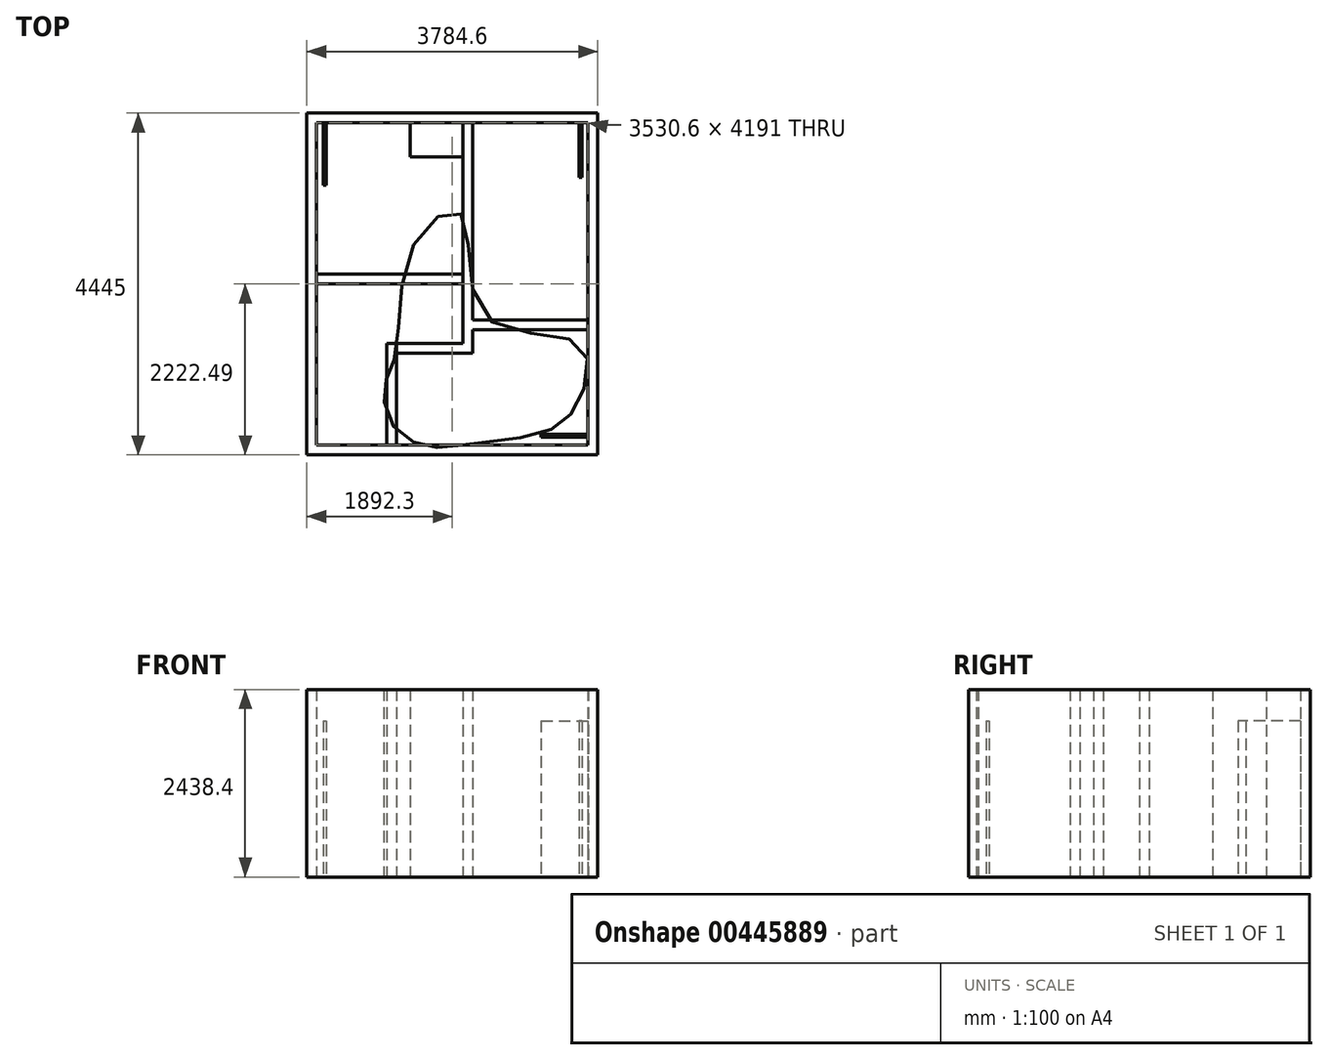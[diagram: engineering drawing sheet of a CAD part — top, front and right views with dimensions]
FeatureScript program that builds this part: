
annotation { "Feature Type Name" : "Feature", "Feature Type Description" : "" }
export const myFeature = defineFeature(function(context is Context, id is Id, definition is map)
    precondition{}
    {
        {
            var Q0;
            Q0=qCreatedBy(makeId("Top.planeOp"),FACE);
            var sketch = newSketch(context, id + "F0", { "sketchPlane" : qUnion([Q0])});
            skLineSegment(sketch, "E0.bottom", {"start": v(-1822.2, 1899.12) * mm, "end": v(1708.4, 1899.12) * mm, "construction": true});
            skLineSegment(sketch, "E0.top", {"start": v(-1822.2, -2291.88) * mm, "end": v(1708.4, -2291.88) * mm, "construction": true});
            skLineSegment(sketch, "E0.left", {"start": v(-1822.2, 1899.12) * mm, "end": v(-1822.2, -2291.88) * mm, "construction": true});
            skLineSegment(sketch, "E0.right", {"start": v(1708.4, 1899.12) * mm, "end": v(1708.4, -2291.88) * mm, "construction": true});
            skLineSegment(sketch, "E1.bottom", {"start": v(-1822.2, 1899.12) * mm, "end": v(1708.4, 1899.12) * mm});
            skLineSegment(sketch, "E1.top", {"start": v(-1822.2, -2291.88) * mm, "end": v(1708.4, -2291.88) * mm});
            skLineSegment(sketch, "E1.left", {"start": v(-1822.2, 1899.12) * mm, "end": v(-1822.2, -2291.88) * mm});
            skLineSegment(sketch, "E1.right", {"start": v(1708.4, 1899.12) * mm, "end": v(1708.4, -2291.88) * mm});
            skLineSegment(sketch, "E2", {"start": v(-1949.2, 2026.12) * mm, "end": v(1835.4, 2026.12) * mm});
            skLineSegment(sketch, "E3", {"start": v(1835.4, 2026.12) * mm, "end": v(1835.4, -2418.88) * mm});
            skLineSegment(sketch, "E4", {"start": v(1835.4, -2418.88) * mm, "end": v(-1949.2, -2418.88) * mm});
            skLineSegment(sketch, "E5", {"start": v(-1949.2, -2418.88) * mm, "end": v(-1949.2, 2026.12) * mm});
            skSolve(sketch);
        }
        {
            var Q0;
            Q0=qCreatedBy(makeId("Top.planeOp"),FACE);
            var sketch = newSketch(context, id + "F1", { "sketchPlane" : qUnion([Q0])});
            skLineSegment(sketch, "E6.bottom", {"start": v(-603, 1899.05) * mm, "end": v(82.8, 1899.05) * mm});
            skLineSegment(sketch, "E6.top", {"start": v(-603, 1454.55) * mm, "end": v(82.8, 1454.55) * mm});
            skLineSegment(sketch, "E6.left", {"start": v(-603, 1899.05) * mm, "end": v(-603, 1454.55) * mm});
            skLineSegment(sketch, "E6.right", {"start": v(82.8, 1899.05) * mm, "end": v(82.8, 1454.55) * mm});
            skSolve(sketch);
        }
        {
            var Q0;
            Q0=qCreatedBy(makeId("Top.planeOp"),FACE);
            var sketch = newSketch(context, id + "F2", { "sketchPlane" : qUnion([Q0])});
            skLineSegment(sketch, "E7.bottom", {"start": v(-907.8, -2291.88) * mm, "end": v(-780.8, -2291.88) * mm});
            skLineSegment(sketch, "E7.top", {"start": v(-907.8, -971.08) * mm, "end": v(-780.8, -971.08) * mm});
            skLineSegment(sketch, "E7.left", {"start": v(-907.8, -2291.88) * mm, "end": v(-907.8, -971.08) * mm});
            skLineSegment(sketch, "E7.right", {"start": v(-780.8, -2291.88) * mm, "end": v(-780.8, -971.08) * mm});
            skSolve(sketch);
        }
        {
            var Q0;
            Q0=qCreatedBy(makeId("Top.planeOp"),FACE);
            var sketch = newSketch(context, id + "F3", { "sketchPlane" : qUnion([Q0])});
            skLineSegment(sketch, "E8.bottom", {"start": v(1708.4, -793.28) * mm, "end": v(82.8, -793.28) * mm});
            skLineSegment(sketch, "E8.top", {"start": v(1708.4, -666.28) * mm, "end": v(82.8, -666.28) * mm});
            skLineSegment(sketch, "E8.left", {"start": v(1708.4, -793.28) * mm, "end": v(1708.4, -666.28) * mm});
            skLineSegment(sketch, "E8.right", {"start": v(82.8, -793.28) * mm, "end": v(82.8, -666.28) * mm});
            skLineSegment(sketch, "E9.bottom", {"start": v(82.8, -666.28) * mm, "end": v(209.8, -666.28) * mm});
            skLineSegment(sketch, "E9.top", {"start": v(82.8, 1899.12) * mm, "end": v(209.8, 1899.12) * mm});
            skLineSegment(sketch, "E9.left", {"start": v(82.8, -666.28) * mm, "end": v(82.8, 1899.12) * mm});
            skLineSegment(sketch, "E9.right", {"start": v(209.8, -666.28) * mm, "end": v(209.8, 1899.12) * mm});
            skLineSegment(sketch, "E10.bottom", {"start": v(-780.8, -971.08) * mm, "end": v(209.8, -971.08) * mm});
            skLineSegment(sketch, "E10.top", {"start": v(-780.8, -1098.08) * mm, "end": v(209.8, -1098.08) * mm});
            skLineSegment(sketch, "E10.left", {"start": v(-780.8, -971.08) * mm, "end": v(-780.8, -1098.08) * mm});
            skLineSegment(sketch, "E10.right", {"start": v(209.8, -971.08) * mm, "end": v(209.8, -1098.08) * mm});
            skLineSegment(sketch, "E11.bottom", {"start": v(82.8, -793.28) * mm, "end": v(209.8, -793.28) * mm});
            skLineSegment(sketch, "E11.top", {"start": v(82.8, -971.08) * mm, "end": v(209.8, -971.08) * mm});
            skLineSegment(sketch, "E11.left", {"start": v(82.8, -793.28) * mm, "end": v(82.8, -971.08) * mm});
            skLineSegment(sketch, "E11.right", {"start": v(209.8, -793.28) * mm, "end": v(209.8, -971.08) * mm});
            skPoint(sketch, "E12.endSnap0", {"position": v(82.8, -882.18) * mm});
            skSolve(sketch);
        }
        {
            var Q0;
            Q0=qCreatedBy(makeId("Top.planeOp"),FACE);
            var sketch = newSketch(context, id + "F4", { "sketchPlane" : qUnion([Q0])});
            skLineSegment(sketch, "E13.bottom", {"start": v(1098.8, -2152.18) * mm, "end": v(1708.4, -2152.18) * mm});
            skLineSegment(sketch, "E13.top", {"start": v(1098.8, -2190.28) * mm, "end": v(1708.4, -2190.28) * mm});
            skLineSegment(sketch, "E13.left", {"start": v(1098.8, -2190.28) * mm, "end": v(1098.8, -2152.18) * mm});
            skLineSegment(sketch, "E13.right", {"start": v(1708.4, -2190.28) * mm, "end": v(1708.4, -2152.18) * mm});
            skArc(sketch, "E14", {"start": v(1098.8, -2190.28) * mm, "mid": v(1277.35, -1759.23) * mm, "end": v(1708.4, -1580.68) * mm});
            skSolve(sketch);
        }
        {
            var Q0;
            Q0=qCreatedBy(makeId("Top.planeOp"),FACE);
            var sketch = newSketch(context, id + "F5", { "sketchPlane" : qUnion([Q0])});
            skLineSegment(sketch, "E15.bottom", {"start": v(1632.2, 1899.12) * mm, "end": v(1594.1, 1899.12) * mm});
            skLineSegment(sketch, "E15.top", {"start": v(1632.2, 1187.92) * mm, "end": v(1594.1, 1187.92) * mm});
            skLineSegment(sketch, "E15.left", {"start": v(1632.2, 1899.12) * mm, "end": v(1632.2, 1187.92) * mm});
            skLineSegment(sketch, "E15.right", {"start": v(1594.1, 1899.12) * mm, "end": v(1594.1, 1187.92) * mm});
            skArc(sketch, "E16", {"start": v(1632.2, 1187.92) * mm, "mid": v(1129.3, 1396.22) * mm, "end": v(921, 1899.12) * mm});
            skSolve(sketch);
        }
        {
            var Q0;
            Q0=qCreatedBy(makeId("Top.planeOp"),FACE);
            var sketch = newSketch(context, id + "F6", { "sketchPlane" : qUnion([Q0])});
            skLineSegment(sketch, "E17.bottom", {"start": v(-1733.3, 1899.05) * mm, "end": v(-1695.2, 1899.05) * mm});
            skLineSegment(sketch, "E17.top", {"start": v(-1733.3, 1086.25) * mm, "end": v(-1695.2, 1086.25) * mm});
            skLineSegment(sketch, "E17.left", {"start": v(-1733.3, 1899.05) * mm, "end": v(-1733.3, 1086.25) * mm});
            skLineSegment(sketch, "E17.right", {"start": v(-1695.2, 1899.05) * mm, "end": v(-1695.2, 1086.25) * mm});
            skArc(sketch, "E18", {"start": v(-1733.3, 1086.25) * mm, "mid": v(-1158.56, 1324.31) * mm, "end": v(-920.5, 1899.05) * mm});
            skSolve(sketch);
        }
        {
            var Q0;
            Q0=qCreatedBy(makeId("Top.planeOp"),FACE);
            var sketch = newSketch(context, id + "F7", { "sketchPlane" : qUnion([Q0])});
            skLineSegment(sketch, "E19.bottom", {"start": v(82.8, -69.45) * mm, "end": v(-1822.2, -69.45) * mm});
            skLineSegment(sketch, "E19.top", {"start": v(82.8, -196.45) * mm, "end": v(-1822.2, -196.45) * mm});
            skLineSegment(sketch, "E19.left", {"start": v(82.8, -69.45) * mm, "end": v(82.8, -196.45) * mm});
            skLineSegment(sketch, "E19.right", {"start": v(-1822.2, -69.45) * mm, "end": v(-1822.2, -196.45) * mm});
            skSolve(sketch);
        }
        {
            var Q0;
            Q0=makeQuery(id+"F0.imprint","IMPRINT",FACE,{"disambiguationData":[TD([[makeQuery(id+"F0.imprint","IMPRINT",EDGE,{"derivedFrom":sQuery(id+"F0.wireOp",EDGE,"E1.bottom")}),-1.0]])]});
            var sketch = newSketch(context, id + "F8", { "sketchPlane" : qUnion([Q0])});
            skFitSpline(sketch, "E20", {"points": [v(53.37, 711.49) * mm, v(-560.87, 314.48) * mm, v(-798.61, -1131.79) * mm, v(-941.14, -1532.65) * mm, v(-794.16, -2084.94) * mm, v(-295.31, -2316.55) * mm, v(167.9, -2276.47) * mm, v(1170.05, -2107.21) * mm, v(1597.64, -1701.9) * mm, v(1602.5, -982.18) * mm, v(360.5, -606.88) * mm, v(53.37, 711.49) * mm]});
            skLineSegment(sketch, "E21", {"start": v(105.12, -1288.17) * mm, "end": v(160.26, -1526.44) * mm});
            skSolve(sketch);
        }
        {
            var Q0;
            Q0 = qSketchRegion(id + "F1", true);
            var Q1;
            Q1 = qSketchRegion(id + "F2", true);
            var Q2;
            Q2 = qSketchRegion(id + "F3", true);
            var Q3;
            Q3 = qSketchRegion(id + "F7", true);
            extrude(context, id + "F9", {"entities" : qUnion([Q0, Q1, Q2, Q3]), "depth" : 2438.4 * mm});
        }
        {
            var Q0;
            Q0 = qSketchRegion(id + "F4", true);
            var Q1;
            Q1 = qSketchRegion(id + "F5", true);
            var Q2;
            Q2 = qSketchRegion(id + "F6", true);
            extrude(context, id + "F10", {"entities" : qUnion([Q0, Q1, Q2]), "depth" : 2032 * mm});
        }
        {
            var Q0;
            Q0 = qSketchRegion(id + "F0", true);
            extrude(context, id + "F11", {"entities" : qUnion([Q0]), "depth" : 2438.4 * mm});
        }
        {
            var Q0;
            Q0 = qSketchRegion(id + "F8", true);
            extrude(context, id + "F12", {"entities" : qUnion([Q0]), "depth" : 2438.4 * mm});
        }
    });
